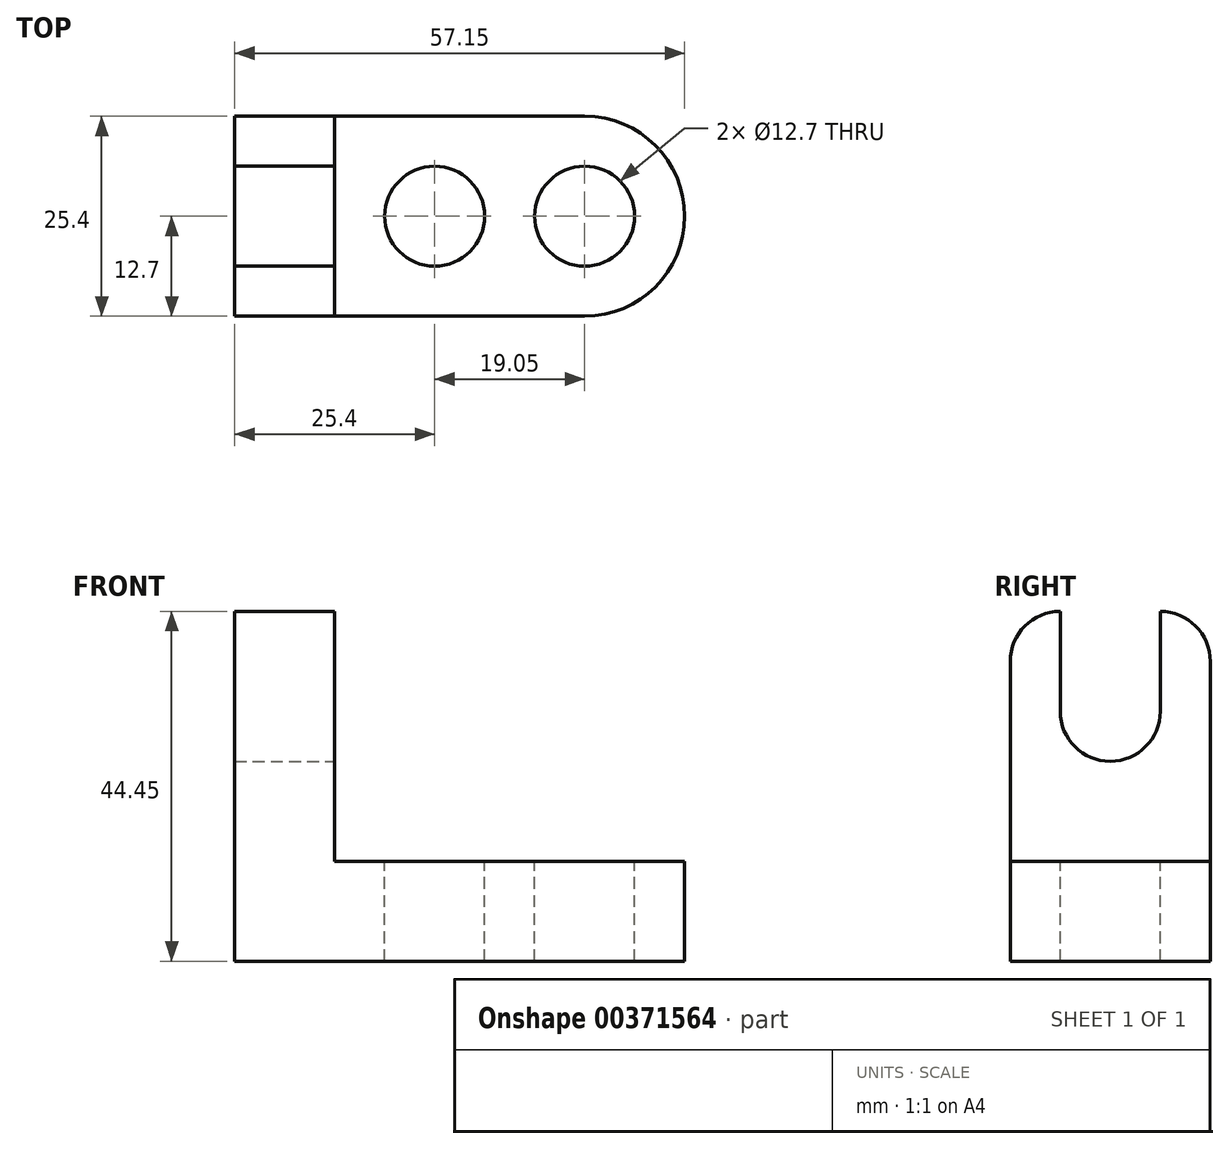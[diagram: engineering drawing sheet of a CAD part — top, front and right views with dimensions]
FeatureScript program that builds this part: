
annotation { "Feature Type Name" : "Feature", "Feature Type Description" : "" }
export const myFeature = defineFeature(function(context is Context, id is Id, definition is map)
    precondition{}
    {
        {
            var Q0;
            Q0=qCreatedBy(makeId("Front.planeOp"),FACE);
            var sketch = newSketch(context, id + "F0", { "sketchPlane" : qUnion([Q0])});
            skLineSegment(sketch, "E0", {"start": v(0, 0) * mm, "end": v(57.15, 0) * mm});
            skLineSegment(sketch, "E1", {"start": v(57.15, 0) * mm, "end": v(57.15, 12.7) * mm});
            skLineSegment(sketch, "E2", {"start": v(57.15, 12.7) * mm, "end": v(12.7, 12.7) * mm});
            skLineSegment(sketch, "E3", {"start": v(12.7, 12.7) * mm, "end": v(12.7, 44.45) * mm});
            skLineSegment(sketch, "E4", {"start": v(12.7, 44.45) * mm, "end": v(0, 44.45) * mm});
            skLineSegment(sketch, "E5", {"start": v(0, 44.45) * mm, "end": v(0, 0) * mm});
            skSolve(sketch);
        }
        {
            var Q0;
            Q0=makeQuery(id+"F0.imprint","IMPRINT",FACE,{"disambiguationData":[TD([[makeQuery(id+"F0.imprint","IMPRINT",EDGE,{"derivedFrom":sQuery(id+"F0.wireOp",EDGE,"E0")}),1.0]])]});
            extrude(context, id + "F1", {"entities" : qUnion([Q0]), "depth" : 25.4 * mm});
        }
        {
            var Q0;
            Q0=makeQuery(id+"F1.opExtrude","SWEPT_FACE",FACE,{"disambiguationData":[OSD([sQuery(id+"F0.wireOp",EDGE,"E2")])]});
            var sketch = newSketch(context, id + "F2", { "sketchPlane" : qUnion([Q0])});
            skCircle(sketch, "E6", {"center": v(44.45, -12.7) * mm, "radius": 6.35 * mm});
            skPoint(sketch, "E6.centerSnap0", {"position": v(57.15, -12.7) * mm});
            skCircle(sketch, "E7", {"center": v(25.4, -12.7) * mm, "radius": 6.35 * mm});
            skPoint(sketch, "E7.centerSnap0", {"position": v(12.7, -12.7) * mm});
            skArc(sketch, "E8", {"start": v(44.45, -25.4) * mm, "mid": v(57.15, -12.7) * mm, "end": v(44.45, 0) * mm});
            skSolve(sketch);
        }
        {
            var Q0;
            {var subQ0=sQuery(id+"F2.wireOp",EDGE,"E8");var subQ1=sQuery(id+"F0.wireOp",EDGE,"E2");var subQ2=makeQuery(id+"F1.opExtrude","CAP_EDGE",EDGE,{"disambiguationData":[OSD([subQ1])],"isStart":true});var subQ3=makeQuery(id+"F2.imprint","INTERSECT",VERTEX,{"derivedFrom":[subQ2,subQ0]});Q0=makeQuery(id+"F2.imprint","IMPRINT",FACE,{"disambiguationData":[TD([[makeQuery(id+"F2.imprint","IMPRINT",EDGE,{"disambiguationData":[TD([[subQ3,1.0]])],"derivedFrom":subQ0}),-1.0]])]});}
            var Q1;
            Q1=makeQuery(id+"F2.imprint","IMPRINT",FACE,{"disambiguationData":[TD([[makeQuery(id+"F2.imprint","IMPRINT",EDGE,{"derivedFrom":sQuery(id+"F2.wireOp",EDGE,"E6")}),1.0]])]});
            var Q2;
            {var subQ0=sQuery(id+"F2.wireOp",EDGE,"E8");var subQ1=sQuery(id+"F0.wireOp",EDGE,"E2");var subQ2=makeQuery(id+"F1.opExtrude","CAP_EDGE",EDGE,{"disambiguationData":[OSD([subQ1])],"isStart":false});var subQ3=makeQuery(id+"F2.imprint","INTERSECT",VERTEX,{"derivedFrom":[subQ2,subQ0]});Q2=makeQuery(id+"F2.imprint","IMPRINT",FACE,{"disambiguationData":[TD([[makeQuery(id+"F2.imprint","IMPRINT",EDGE,{"disambiguationData":[TD([[subQ3,-1.0]])],"derivedFrom":subQ0}),-1.0]])]});}
            var Q3;
            Q3=makeQuery(id+"F2.imprint","IMPRINT",FACE,{"disambiguationData":[TD([[makeQuery(id+"F2.imprint","IMPRINT",EDGE,{"derivedFrom":sQuery(id+"F2.wireOp",EDGE,"E7")}),1.0]])]});
            extrude(context, id + "F3", {"entities" : qUnion([Q0, Q1, Q2, Q3]), "operationType" : NewBodyOperationType.REMOVE, "oppositeDirection" : true, "depth" : 25.4 * mm});
        }
        {
            var Q0;
            Q0=makeQuery(id+"F1.opExtrude","SWEPT_FACE",FACE,{"disambiguationData":[OSD([sQuery(id+"F0.wireOp",EDGE,"E3")])]});
            var sketch = newSketch(context, id + "F4", { "sketchPlane" : qUnion([Q0])});
            skCircle(sketch, "E9", {"center": v(-12.7, 31.75) * mm, "radius": 6.35 * mm});
            skPoint(sketch, "E9.centerSnap0", {"position": v(-12.7, 44.45) * mm});
            skLineSegment(sketch, "E10", {"start": v(-19.05, 31.75) * mm, "end": v(-19.05, 44.45) * mm});
            skLineSegment(sketch, "E11", {"start": v(-6.35, 31.75) * mm, "end": v(-6.35, 44.45) * mm});
            skSolve(sketch);
        }
        {
            var Q0;
            {var subQ0=sQuery(id+"F4.wireOp",EDGE,"E10");Q0=makeQuery(id+"F4.imprint","IMPRINT",FACE,{"disambiguationData":[TD([[makeQuery(id+"F4.imprint","IMPRINT",EDGE,{"derivedFrom":subQ0}),-1.0]])]});}
            var Q1;
            {var subQ0=sQuery(id+"F4.wireOp",EDGE,"E9");var subQ1=makeQuery(id+"F4.imprint","INTERSECT",VERTEX,{"derivedFrom":[subQ0,sQuery(id+"F4.wireOp",EDGE,"E10")]});Q1=makeQuery(id+"F4.imprint","IMPRINT",FACE,{"disambiguationData":[TD([[makeQuery(id+"F4.imprint","IMPRINT",EDGE,{"disambiguationData":[TD([[subQ1,1.0]])],"derivedFrom":subQ0}),1.0]])]});}
            extrude(context, id + "F5", {"entities" : qUnion([Q0, Q1]), "operationType" : NewBodyOperationType.REMOVE, "oppositeDirection" : true, "depth" : 25.4 * mm});
        }
        {
            var Q0;
            Q0=makeQuery(id+"F1.opExtrude","SWEPT_FACE",FACE,{"disambiguationData":[OSD([sQuery(id+"F0.wireOp",EDGE,"E3")])]});
            var sketch = newSketch(context, id + "F6", { "sketchPlane" : qUnion([Q0])});
            skArc(sketch, "E12", {"start": v(-19.05, 44.45) * mm, "mid": v(-23.54, 42.6) * mm, "end": v(-25.4, 38.1) * mm});
            skPoint(sketch, "E12.endSnap0", {"position": v(-19.05, 38.1) * mm});
            skArc(sketch, "E13", {"start": v(0, 38.1) * mm, "mid": v(-1.86, 42.6) * mm, "end": v(-6.35, 44.45) * mm});
            skPoint(sketch, "E13.startSnap0", {"position": v(-6.35, 38.1) * mm});
            skSolve(sketch);
        }
        {
            var Q0;
            {var subQ0=sQuery(id+"F6.wireOp",EDGE,"E12");Q0=makeQuery(id+"F6.imprint","IMPRINT",FACE,{"disambiguationData":[TD([[makeQuery(id+"F6.imprint","IMPRINT",EDGE,{"derivedFrom":subQ0}),-1.0]])]});}
            var Q1;
            {var subQ0=sQuery(id+"F6.wireOp",EDGE,"E13");Q1=makeQuery(id+"F6.imprint","IMPRINT",FACE,{"disambiguationData":[TD([[makeQuery(id+"F6.imprint","IMPRINT",EDGE,{"derivedFrom":subQ0}),-1.0]])]});}
            extrude(context, id + "F7", {"entities" : qUnion([Q0, Q1]), "operationType" : NewBodyOperationType.REMOVE, "oppositeDirection" : true, "depth" : 25.4 * mm});
        }
    });
